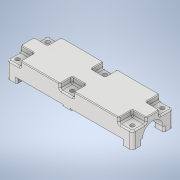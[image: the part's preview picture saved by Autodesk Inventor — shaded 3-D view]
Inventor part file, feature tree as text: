
AUTODESK INVENTOR PART (.ipt)
format: ipt  version: 2022 (Build 260153000, 153)  size: 1,107,456 bytes
history: native  units: mm
features: sketch x16, extrude x15, projected_geometry x10, other x4, fillet x3, boolean_combine x2, mirror x1
ambient origin geometry x8: Origin, YZ Plane, XZ Plane, XY Plane, X Axis, Y Axis, Z Axis, Center Point
bodies: Volumenkörper1 (feature_tree), Solid2 (feature_tree), Solid3 (feature_tree), Solid4 (feature_tree)
feature tree (51):
  other  "rolinho.ipt"
  extrude  "Extrusion1"  Depth=11.0mm
  other  "Spirale1"
  mirror  "Spiegeln1"
  extrude  "Extrusion5"  Depth=4.0mm
  extrude  "Extrusion6"  Depth=1.0mm
  boolean_combine  "Combine1"
  extrude  "Extrusion7"  Depth=10.0mm TaperAngle=0.0deg
  extrude  "Extrusion8"  Depth=100.0mm TaperAngle=0.0deg
  extrude  "Extrusion9"  Depth=24.0mm
  extrude  "Extrusion10"  Depth=12.0mm TaperAngle=0.0deg
  extrude  "Extrusion11"  Depth=4.0mm
  extrude  "Extrusion13"  Depth=20.0mm
  fillet  "Fillet2"  Radius=10.0mm
  fillet  "Fillet3"  Radius=77.15mm
  fillet  "Fillet4"  Radius=30.0mm
  extrude  "Extrusion14"  Depth=6.0mm
  extrude  "Extrusion15"  Depth=10.0mm TaperAngle=0.0deg
  extrude  "Extrusion16"  Depth=3.0mm
  extrude  "Extrusion17"  Depth=48.0mm
  extrude  "Extrusion19"  Depth=4.0mm
  extrude  "Extrusion20"  Depth=0.5mm
  boolean_combine  "Combine2"
  sketch  "Skizze1"  dims[d0=6.0mm d1=11.0mm]
  sketch  "Skizze3"  dims[d2=36.0mm d3=0.0mm]
  projected_geometry  "Projizierte Kontur2"
  sketch  "Sketch7"  dims[d8=7.0mm d9=24.5mm d10=10.0mm d11=0.0mm d12=90.0deg d13=90.0deg d14=0.0mm d15=0.0mm d16=4.0mm]
  sketch  "Sketch8"  dims[d17=13.962634mm d18=1.0mm]
  sketch  "Sketch9"  dims[d19=0.1mm d32=10.0mm d33=0.0mm]
  projected_geometry  "Projected Loop4"
  sketch  "Sketch10"  dims[d34=7.0mm d35=100.0mm d36=0.0mm]
  sketch  "Sketch11"  dims[d37=82.0mm d38=0.0mm d39=24.0mm]
  projected_geometry  "Projected Loop5"
  projected_geometry  "Projected Loop6"
  sketch  "Sketch12"  dims[d40=30.0mm d41=12.0mm d42=0.0mm]
  sketch  "Sketch13"  dims[d43=3.0mm d44=4.0mm]
  projected_geometry  "Projected Loop7"
  projected_geometry  "Projected Loop8"
  sketch  "Sketch15"  dims[d45=4.0mm d46=20.0mm d48=22.0mm d49=20.0mm d51=84.0mm d54=10.0mm d55=0.0mm d56=77.15mm d57=30.0mm]
  sketch  "Sketch16"  dims[d62=4.0mm d63=0.0mm d64=6.0mm]
  projected_geometry  "Projected Loop10"
  sketch  "Sketch17"  dims[d65=10.0mm d66=0.0mm d67=10.0mm d68=0.0mm]
  projected_geometry  "Projected Loop11"
  projected_geometry  "Projected Loop12"
  sketch  "Sketch18"  dims[d76=3.0mm d77=3.0mm]
  sketch  "Sketch19"  dims[d78=4.0mm d79=48.0mm]
  sketch  "Sketch21"  dims[d80=46.0mm d81=4.0mm]
  projected_geometry  "Projected Loop13"
  sketch  "Sketch22"  dims[d85=7.0mm d86=6.9mm d87=3.5mm d88=7.0mm d89=6.9mm d90=3.5mm d91=10.0mm d92=10.0mm d93=10.0mm d94=10.0mm d95=10.0mm d96=10.0mm d97=10.0mm d98=10.0mm d99=10.0mm d100=10.0mm d101=10.0mm d102=10.0mm d103=4.0mm d104=0.0mm d105=1.0mm d106=1.0mm d107=2.0mm d108=0.5mm d109=6.5mm d110=2.1mm d111=0.0mm d112=6.5mm d113=2.1mm d114=0.0mm d115=180.0deg d116=6.9mm d117=6.9mm d118=6.9mm d119=6.9mm d120=12.0mm d121=0.2mm d122=0.0mm d123=15.0mm d124=0.2mm d125=0.0mm d126=7.9mm d127=0.0mm d128=7.9mm d129=0.0mm d132=3.0mm d133=0.0mm d134=13.0mm d135=10.0mm d136=0.0mm d137=10.0mm]
  other  "Solid1::rolinho.ipt"
  other  "TaggingFeature1"
